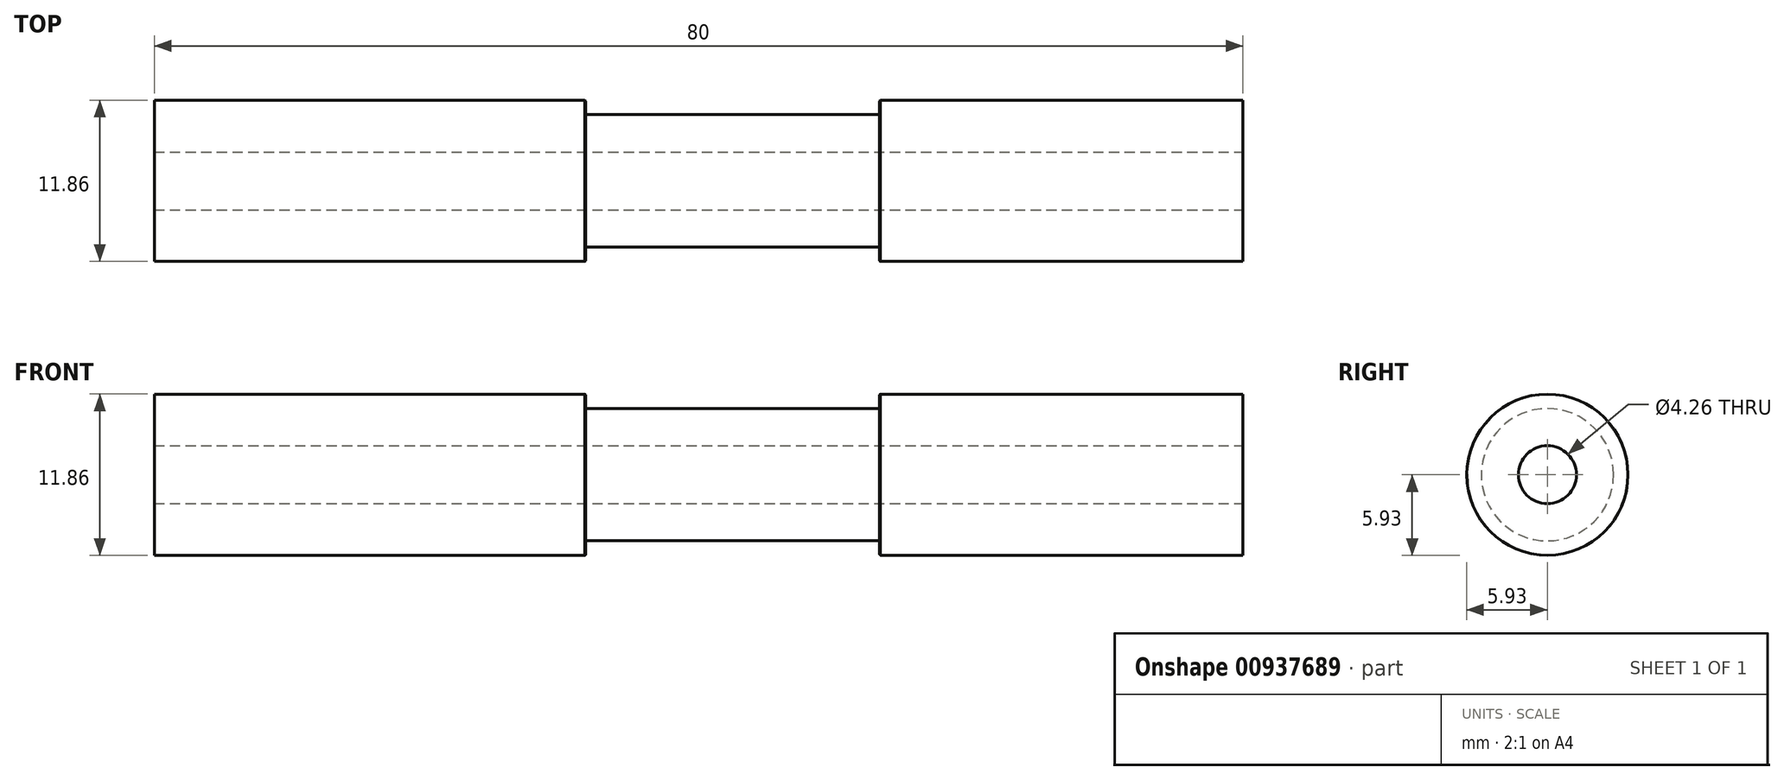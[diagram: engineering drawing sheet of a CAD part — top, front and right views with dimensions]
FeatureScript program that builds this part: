
annotation { "Feature Type Name" : "Feature", "Feature Type Description" : "" }
export const myFeature = defineFeature(function(context is Context, id is Id, definition is map)
    precondition{}
    {
        {
            var Q0;
            Q0=qCreatedBy(makeId("Right.planeOp"),FACE);
            var sketch = newSketch(context, id + "F0", { "sketchPlane" : qUnion([Q0])});
            skCircle(sketch, "E0", {"center": v(0, 0) * mm, "radius": 5.92 * mm});
            skSolve(sketch);
        }
        {
            var Q0;
            Q0=makeQuery(id+"F0.imprint","IMPRINT",FACE,{"disambiguationData":[TD([[makeQuery(id+"F0.imprint","IMPRINT",EDGE,{"derivedFrom":sQuery(id+"F0.wireOp",EDGE,"E0")}),1.0]])]});
            var Q1;
            Q1=sQuery(id+"F0.wireOp",EDGE,"E0");
            extrude(context, id + "F1", {"entities" : qUnion([Q0]), "surfaceEntities" : qUnion([Q1]), "depth" : 31.7 * mm, "offsetDistance" : 25 * mm});
        }
        {
            var Q0;
            Q0=makeQuery(id+"F1.opExtrude","CAP_FACE",FACE,{"disambiguationData":[OSD([sQuery(id+"F0.wireOp",EDGE,"E0")])],"isStart":false});
            var sketch = newSketch(context, id + "F2", { "sketchPlane" : qUnion([Q0])});
            skCircle(sketch, "E1", {"center": v(0, 0) * mm, "radius": 4.87 * mm});
            skSolve(sketch);
        }
        {
            var Q0;
            Q0=makeQuery(id+"F2.imprint","IMPRINT",FACE,{"disambiguationData":[TD([[makeQuery(id+"F2.imprint","IMPRINT",EDGE,{"derivedFrom":sQuery(id+"F2.wireOp",EDGE,"E1")}),1.0]])]});
            var Q1;
            Q1=sQuery(id+"F2.wireOp",EDGE,"E1");
            extrude(context, id + "F3", {"entities" : qUnion([Q0]), "operationType" : NewBodyOperationType.ADD, "surfaceEntities" : qUnion([Q1]), "depth" : 21.6 * mm, "offsetDistance" : 25 * mm});
        }
        {
            var Q0;
            Q0=makeQuery(id+"F3.opExtrude","CAP_FACE",FACE,{"disambiguationData":[OSD([sQuery(id+"F2.wireOp",EDGE,"E1")])],"isStart":false});
            var sketch = newSketch(context, id + "F4", { "sketchPlane" : qUnion([Q0])});
            skCircle(sketch, "E2", {"center": v(0, 0) * mm, "radius": 5.92 * mm});
            skSolve(sketch);
        }
        {
            var Q0;
            Q0=makeQuery(id+"F4.imprint","IMPRINT",FACE,{"disambiguationData":[TD([[makeQuery(id+"F4.imprint","IMPRINT",EDGE,{"derivedFrom":sQuery(id+"F4.wireOp",EDGE,"E2")}),1.0]])]});
            var Q1;
            Q1=makeQuery(id+"F4.imprint","IMPRINT",FACE,{"disambiguationData":[TD([[makeQuery(id+"F4.imprint","IMPRINT",EDGE,{"derivedFrom":makeQuery(id+"F3.opExtrude","CAP_EDGE",EDGE,{"disambiguationData":[OSD([sQuery(id+"F2.wireOp",EDGE,"E1")])],"isStart":false})}),1.0]])]});
            var Q2;
            Q2=sQuery(id+"F4.wireOp",EDGE,"E2");
            extrude(context, id + "F5", {"entities" : qUnion([Q0, Q1]), "operationType" : NewBodyOperationType.ADD, "surfaceEntities" : qUnion([Q2]), "depth" : 26.7 * mm, "offsetDistance" : 25 * mm});
        }
        {
            var Q0;
            Q0=makeQuery(id+"F5.opExtrude","CAP_FACE",FACE,{"disambiguationData":[OSD([sQuery(id+"F4.wireOp",EDGE,"E2")])],"isStart":false});
            var sketch = newSketch(context, id + "F6", { "sketchPlane" : qUnion([Q0])});
            skCircle(sketch, "E3", {"center": v(0, 0) * mm, "radius": 2.13 * mm});
            skSolve(sketch);
        }
        {
            var Q0;
            Q0=sQuery(id+"F6.wireOp",VERTEX,"E3.center");
            var Q1;
            Q1=makeQuery(id+"F1.opExtrude","SWEPT_BODY",BODY,{"disambiguationData":[OSD([sQuery(id+"F0.wireOp",EDGE,"E0")])]});
            hole(context, id + "F7", {"style" : HoleStyle.SIMPLE, "endStyle" : HoleEndStyle.THROUGH, "holeDiameter" : 4.26 * mm, "majorDiameter" : 5 * mm, "isTappedThrough" : true, "tappedDepth" : 12 * mm, "tapClearance" : 3, "locations" : qUnion([Q0]), "scope" : qUnion([Q1])});
        }
        {
            var Q0;
            Q0=makeQuery(id+"F1.opExtrude","CAP_EDGE",EDGE,{"disambiguationData":[OSD([sQuery(id+"F0.wireOp",EDGE,"E0")])],"isStart":false});
            chamfer(context, id + "F8", {"entities" : qUnion([Q0]), "width" : 0.05 * mm, "tangentPropagation" : true});
        }
        {
            var Q0;
            Q0=makeQuery(id+"F5.opExtrude","CAP_EDGE",EDGE,{"disambiguationData":[OSD([sQuery(id+"F4.wireOp",EDGE,"E2")])],"isStart":true});
            chamfer(context, id + "F9", {"entities" : qUnion([Q0]), "width" : 0.05 * mm, "tangentPropagation" : true});
        }
    });
